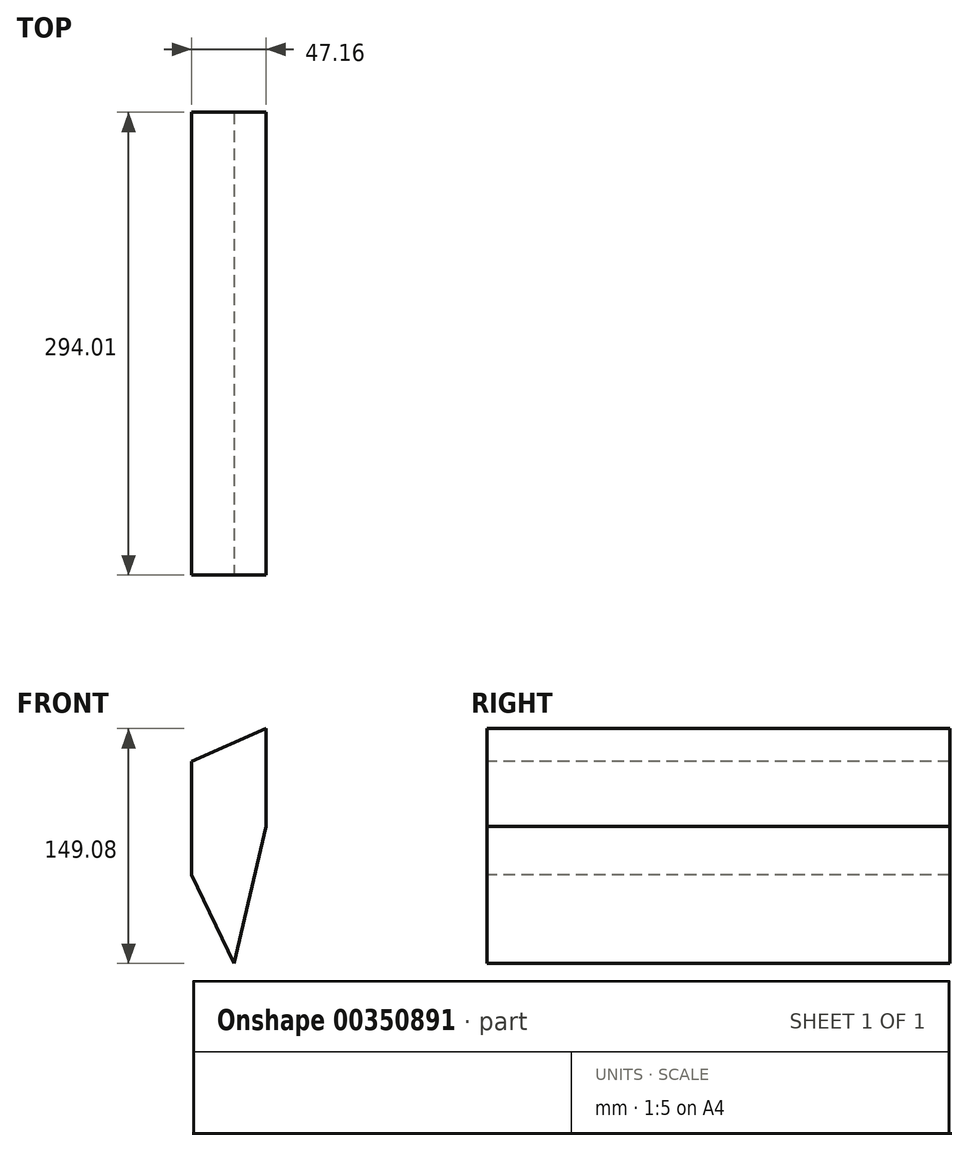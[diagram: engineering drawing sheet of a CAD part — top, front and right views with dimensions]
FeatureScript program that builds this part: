
annotation { "Feature Type Name" : "Feature", "Feature Type Description" : "" }
export const myFeature = defineFeature(function(context is Context, id is Id, definition is map)
    precondition{}
    {
        {
            var Q0;
            Q0=qCreatedBy(makeId("Front.planeOp"),FACE);
            var sketch = newSketch(context, id + "F0", { "sketchPlane" : qUnion([Q0])});
            skLineSegment(sketch, "E0", {"start": v(0, 62.01) * mm, "end": v(-47.16, 41.25) * mm});
            skLineSegment(sketch, "E1", {"start": v(-47.16, 41.25) * mm, "end": v(-47.16, -30.85) * mm});
            skLineSegment(sketch, "E2", {"start": v(-47.16, -30.85) * mm, "end": v(-20.36, -87.07) * mm});
            skLineSegment(sketch, "E3", {"start": v(-20.36, -87.07) * mm, "end": v(0, 0) * mm});
            skLineSegment(sketch, "E4", {"start": v(0, 0) * mm, "end": v(0, 62.01) * mm});
            skSolve(sketch);
        }
        {
            var Q0;
            Q0=makeQuery(id+"F0.imprint","IMPRINT",FACE,{"disambiguationData":[TD([[makeQuery(id+"F0.imprint","IMPRINT",EDGE,{"derivedFrom":sQuery(id+"F0.wireOp",EDGE,"E0")}),1.0]])]});
            extrude(context, id + "F1", {"entities" : qUnion([Q0]), "oppositeDirection" : true, "depth" : 294 * mm});
        }
    });
